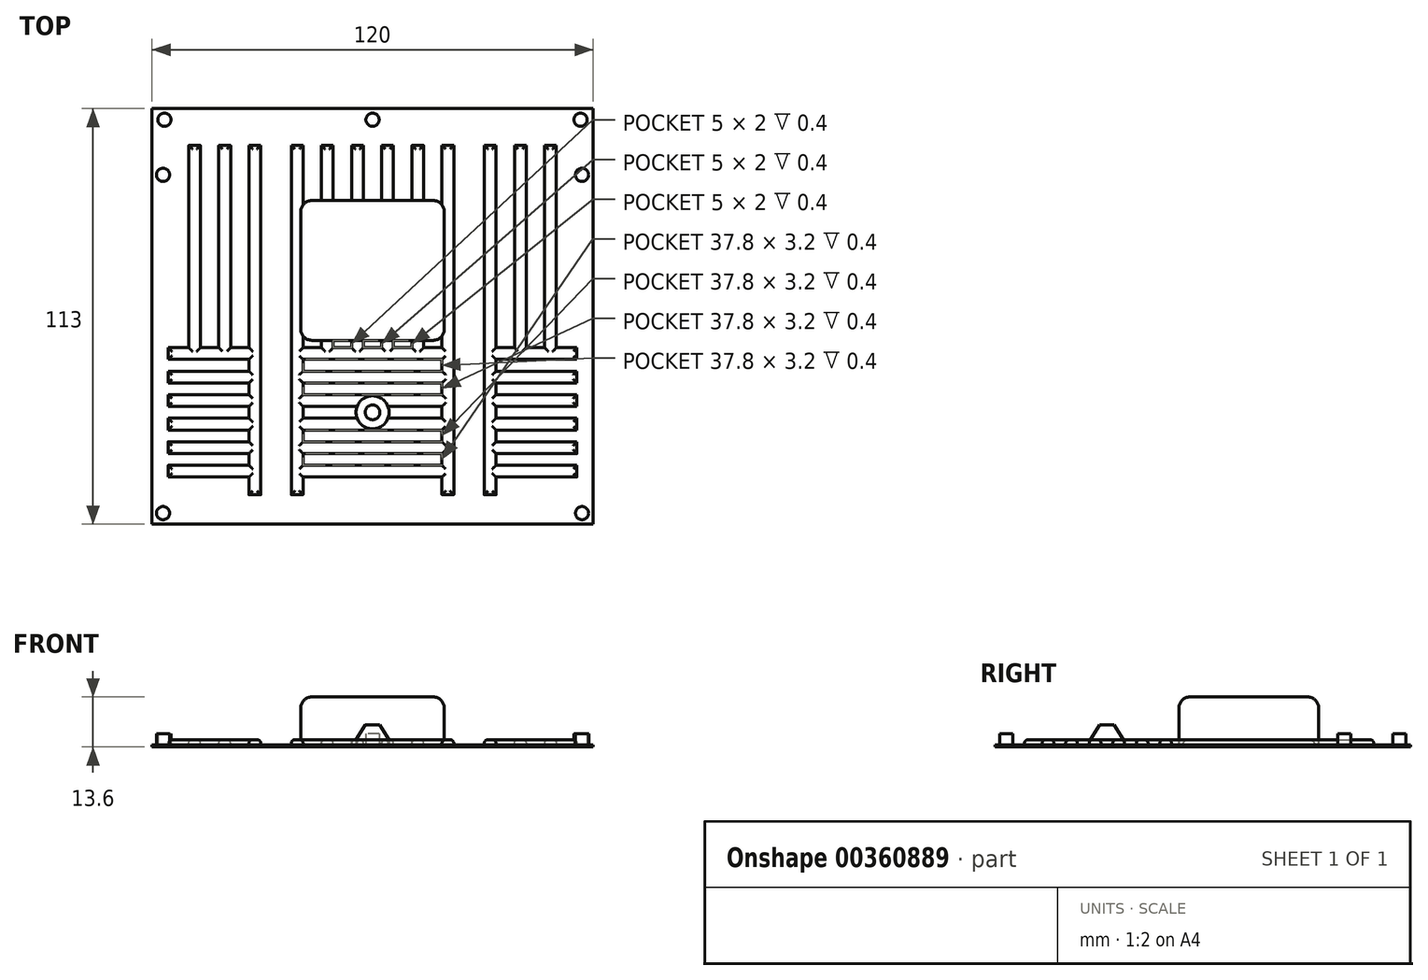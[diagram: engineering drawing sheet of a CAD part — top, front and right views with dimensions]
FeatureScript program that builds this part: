
annotation { "Feature Type Name" : "Feature", "Feature Type Description" : "" }
export const myFeature = defineFeature(function(context is Context, id is Id, definition is map)
    precondition{}
    {
        {
            var Q0;
            Q0=qCreatedBy(makeId("Top.planeOp"),FACE);
            var sketch = newSketch(context, id + "F0", { "sketchPlane" : qUnion([Q0])});
            skLineSegment(sketch, "E0.bottom", {"start": v(-60, 0) * mm, "end": v(60, 0) * mm});
            skLineSegment(sketch, "E0.top", {"start": v(-60, -113) * mm, "end": v(60, -113) * mm});
            skLineSegment(sketch, "E0.left", {"start": v(-60, 0) * mm, "end": v(-60, -113) * mm});
            skLineSegment(sketch, "E0.right", {"start": v(60, 0) * mm, "end": v(60, -113) * mm});
            skPoint(sketch, "E1", {"position": v(0, 0) * mm});
            skSolve(sketch);
        }
        {
            var Q0;
            Q0 = qSketchRegion(id + "F0", true);
            extrude(context, id + "F1", {"entities" : qUnion([Q0]), "depth" : 0.6 * mm});
        }
        {
            var Q0;
            Q0=qCreatedBy(makeId("Front.planeOp"),FACE);
            cPlane(context, id + "F2", {"entities" : qUnion([Q0]), "cplaneType" : CPlaneType.OFFSET, "offset" : 10 * mm, "width" : 150 * mm, "height" : 150 * mm});
        }
        {
            var Q0;
            {var subQ37=sQuery(id+"F0.wireOp",EDGE,"E0.bottom");var subQ42=sQuery(id+"F0.wireOp",EDGE,"E0.right");var subQ43=sQuery(id+"F0.wireOp",EDGE,"E0.top");var subQ45=sQuery(id+"F0.wireOp",EDGE,"E0.left");Q0=makeQuery(id+"F12.boolean.opBoolean","SPLIT",FACE,{"disambiguationData":[TD([makeQuery(id+"F1.opExtrude","SWEPT_FACE",FACE,{"disambiguationData":[OSD([subQ37])]})])],"derivedFrom":makeQuery(id+"F1.opExtrude","CAP_FACE",FACE,{"disambiguationData":[OSD([subQ37,subQ43,subQ45,subQ42])],"isStart":false})});}
            var sketch = newSketch(context, id + "F3", { "sketchPlane" : qUnion([Q0])});
            skLineSegment(sketch, "E2.bottom", {"start": v(-19.5, -25) * mm, "end": v(19.5, -25) * mm});
            skLineSegment(sketch, "E2.top", {"start": v(-19.5, -63) * mm, "end": v(19.5, -63) * mm});
            skLineSegment(sketch, "E2.left", {"start": v(-19.5, -25) * mm, "end": v(-19.5, -63) * mm});
            skLineSegment(sketch, "E2.right", {"start": v(19.5, -25) * mm, "end": v(19.5, -63) * mm});
            skSolve(sketch);
        }
        {
            var Q0;
            Q0=qCreatedBy(id+"F2.planeOp",FACE);
            var sketch = newSketch(context, id + "F4", { "sketchPlane" : qUnion([Q0])});
            skLineSegment(sketch, "E3.bottom", {"start": v(50, 0.6) * mm, "end": v(46.8, 0.6) * mm});
            skLineSegment(sketch, "E3.top", {"start": v(50, 2) * mm, "end": v(46.8, 2) * mm});
            skLineSegment(sketch, "E3.left", {"start": v(50, 0.6) * mm, "end": v(50, 2) * mm});
            skLineSegment(sketch, "E3.right", {"start": v(46.8, 0.6) * mm, "end": v(46.8, 2) * mm});
            skLineSegment(sketch, "E4.bottom", {"start": v(41.8, 2) * mm, "end": v(38.6, 2) * mm});
            skLineSegment(sketch, "E4.top", {"start": v(41.8, 0.6) * mm, "end": v(38.6, 0.6) * mm});
            skLineSegment(sketch, "E4.left", {"start": v(41.8, 2) * mm, "end": v(41.8, 0.6) * mm});
            skLineSegment(sketch, "E4.right", {"start": v(38.6, 2) * mm, "end": v(38.6, 0.6) * mm});
            skLineSegment(sketch, "E5.bottom", {"start": v(33.6, 2) * mm, "end": v(30.4, 2) * mm});
            skLineSegment(sketch, "E5.top", {"start": v(33.6, 0.6) * mm, "end": v(30.4, 0.6) * mm});
            skLineSegment(sketch, "E5.left", {"start": v(33.6, 2) * mm, "end": v(33.6, 0.6) * mm});
            skLineSegment(sketch, "E5.right", {"start": v(30.4, 2) * mm, "end": v(30.4, 0.6) * mm});
            skLineSegment(sketch, "E6.bottom", {"start": v(-46.8, 2) * mm, "end": v(-50, 2) * mm});
            skLineSegment(sketch, "E6.top", {"start": v(-46.8, 0.6) * mm, "end": v(-50, 0.6) * mm});
            skLineSegment(sketch, "E6.left", {"start": v(-46.8, 2) * mm, "end": v(-46.8, 0.6) * mm});
            skLineSegment(sketch, "E6.right", {"start": v(-50, 2) * mm, "end": v(-50, 0.6) * mm});
            skLineSegment(sketch, "E7.bottom", {"start": v(-38.6, 2) * mm, "end": v(-41.8, 2) * mm});
            skLineSegment(sketch, "E7.top", {"start": v(-38.6, 0.6) * mm, "end": v(-41.8, 0.6) * mm});
            skLineSegment(sketch, "E7.left", {"start": v(-38.6, 2) * mm, "end": v(-38.6, 0.6) * mm});
            skLineSegment(sketch, "E7.right", {"start": v(-41.8, 2) * mm, "end": v(-41.8, 0.6) * mm});
            skLineSegment(sketch, "E8.bottom", {"start": v(-30.4, 2) * mm, "end": v(-33.6, 2) * mm});
            skLineSegment(sketch, "E8.top", {"start": v(-30.4, 0.6) * mm, "end": v(-33.6, 0.6) * mm});
            skLineSegment(sketch, "E8.left", {"start": v(-30.4, 2) * mm, "end": v(-30.4, 0.6) * mm});
            skLineSegment(sketch, "E8.right", {"start": v(-33.6, 2) * mm, "end": v(-33.6, 0.6) * mm});
            skLineSegment(sketch, "E9.bottom", {"start": v(-2.5, 2) * mm, "end": v(-5.7, 2) * mm});
            skLineSegment(sketch, "E9.top", {"start": v(-2.5, 0.6) * mm, "end": v(-5.7, 0.6) * mm});
            skLineSegment(sketch, "E9.left", {"start": v(-2.5, 2) * mm, "end": v(-2.5, 0.6) * mm});
            skLineSegment(sketch, "E9.right", {"start": v(-5.7, 2) * mm, "end": v(-5.7, 0.6) * mm});
            skLineSegment(sketch, "E10.bottom", {"start": v(-10.7, 2) * mm, "end": v(-13.9, 2) * mm});
            skLineSegment(sketch, "E10.top", {"start": v(-10.7, 0.6) * mm, "end": v(-13.9, 0.6) * mm});
            skLineSegment(sketch, "E10.left", {"start": v(-10.7, 2) * mm, "end": v(-10.7, 0.6) * mm});
            skLineSegment(sketch, "E10.right", {"start": v(-13.9, 2) * mm, "end": v(-13.9, 0.6) * mm});
            skLineSegment(sketch, "E11.bottom", {"start": v(-18.9, 2) * mm, "end": v(-22.1, 2) * mm});
            skLineSegment(sketch, "E11.top", {"start": v(-18.9, 0.6) * mm, "end": v(-22.1, 0.6) * mm});
            skLineSegment(sketch, "E11.left", {"start": v(-18.9, 2) * mm, "end": v(-18.9, 0.6) * mm});
            skLineSegment(sketch, "E11.right", {"start": v(-22.1, 2) * mm, "end": v(-22.1, 0.6) * mm});
            skLineSegment(sketch, "E12.bottom", {"start": v(5.7, 2) * mm, "end": v(2.5, 2) * mm});
            skLineSegment(sketch, "E12.top", {"start": v(5.7, 0.6) * mm, "end": v(2.5, 0.6) * mm});
            skLineSegment(sketch, "E12.left", {"start": v(5.7, 2) * mm, "end": v(5.7, 0.6) * mm});
            skLineSegment(sketch, "E12.right", {"start": v(2.5, 2) * mm, "end": v(2.5, 0.6) * mm});
            skLineSegment(sketch, "E13.bottom", {"start": v(13.9, 2) * mm, "end": v(10.7, 2) * mm});
            skLineSegment(sketch, "E13.top", {"start": v(13.9, 0.6) * mm, "end": v(10.7, 0.6) * mm});
            skLineSegment(sketch, "E13.left", {"start": v(13.9, 2) * mm, "end": v(13.9, 0.6) * mm});
            skLineSegment(sketch, "E13.right", {"start": v(10.7, 2) * mm, "end": v(10.7, 0.6) * mm});
            skLineSegment(sketch, "E14.bottom", {"start": v(22.1, 2) * mm, "end": v(18.9, 2) * mm});
            skLineSegment(sketch, "E14.top", {"start": v(22.1, 0.6) * mm, "end": v(18.9, 0.6) * mm});
            skLineSegment(sketch, "E14.left", {"start": v(22.1, 2) * mm, "end": v(22.1, 0.6) * mm});
            skLineSegment(sketch, "E14.right", {"start": v(18.9, 2) * mm, "end": v(18.9, 0.6) * mm});
            skSolve(sketch);
        }
        {
            var Q0;
            Q0 = qSketchRegion(id + "F4", true);
            extrude(context, id + "F5", {"entities" : qUnion([Q0]), "operationType" : NewBodyOperationType.ADD, "depth" : 55 * mm});
        }
        {
            var Q0;
            Q0=makeQuery(id+"F5.opExtrude","CAP_FACE",FACE,{"disambiguationData":[OSD([sQuery(id+"F4.wireOp",EDGE,"E8.bottom"),sQuery(id+"F4.wireOp",EDGE,"E8.top"),sQuery(id+"F4.wireOp",EDGE,"E8.left"),sQuery(id+"F4.wireOp",EDGE,"E8.right")])],"isStart":true});
            var Q1;
            Q1=makeQuery(id+"F5.opExtrude","CAP_FACE",FACE,{"disambiguationData":[OSD([sQuery(id+"F4.wireOp",EDGE,"E11.bottom"),sQuery(id+"F4.wireOp",EDGE,"E11.top"),sQuery(id+"F4.wireOp",EDGE,"E11.left"),sQuery(id+"F4.wireOp",EDGE,"E11.right")])],"isStart":true});
            var Q2;
            Q2=makeQuery(id+"F5.opExtrude","CAP_FACE",FACE,{"disambiguationData":[OSD([sQuery(id+"F4.wireOp",EDGE,"E14.bottom"),sQuery(id+"F4.wireOp",EDGE,"E14.top"),sQuery(id+"F4.wireOp",EDGE,"E14.left"),sQuery(id+"F4.wireOp",EDGE,"E14.right")])],"isStart":true});
            var Q3;
            Q3=makeQuery(id+"F5.opExtrude","CAP_FACE",FACE,{"disambiguationData":[OSD([sQuery(id+"F4.wireOp",EDGE,"E5.bottom"),sQuery(id+"F4.wireOp",EDGE,"E5.top"),sQuery(id+"F4.wireOp",EDGE,"E5.left"),sQuery(id+"F4.wireOp",EDGE,"E5.right")])],"isStart":true});
            extrude(context, id + "F6", {"entities" : qUnion([Q0, Q1, Q2, Q3]), "operationType" : NewBodyOperationType.ADD, "oppositeDirection" : true, "depth" : 95 * mm});
        }
        {
            var Q0;
            {var subQ0=sQuery(id+"F4.wireOp",EDGE,"E8.right");Q0=makeQuery(id+"F6.boolean.opBoolean","MERGE",FACE,{"derivedFrom":[makeQuery(id+"F5.opExtrude","SWEPT_FACE",FACE,{"disambiguationData":[OSD([subQ0])]}),makeQuery(id+"F6.opExtrude","SWEPT_FACE",FACE,{"disambiguationData":[OSD([subQ0])]})]});}
            var sketch = newSketch(context, id + "F7", { "sketchPlane" : qUnion([Q0])});
            skLineSegment(sketch, "E15.bottom", {"start": v(65, 2) * mm, "end": v(68.2, 2) * mm});
            skLineSegment(sketch, "E15.top", {"start": v(65, 0.6) * mm, "end": v(68.2, 0.6) * mm});
            skLineSegment(sketch, "E15.left", {"start": v(65, 2) * mm, "end": v(65, 0.6) * mm});
            skLineSegment(sketch, "E15.right", {"start": v(68.2, 2) * mm, "end": v(68.2, 0.6) * mm});
            skLineSegment(sketch, "E16.bottom", {"start": v(71.4, 2) * mm, "end": v(74.6, 2) * mm});
            skLineSegment(sketch, "E16.top", {"start": v(71.4, 0.6) * mm, "end": v(74.6, 0.6) * mm});
            skLineSegment(sketch, "E16.left", {"start": v(71.4, 2) * mm, "end": v(71.4, 0.6) * mm});
            skLineSegment(sketch, "E16.right", {"start": v(74.6, 2) * mm, "end": v(74.6, 0.6) * mm});
            skLineSegment(sketch, "E17.bottom", {"start": v(77.8, 2) * mm, "end": v(81, 2) * mm});
            skLineSegment(sketch, "E17.top", {"start": v(77.8, 0.6) * mm, "end": v(81, 0.6) * mm});
            skLineSegment(sketch, "E17.left", {"start": v(77.8, 2) * mm, "end": v(77.8, 0.6) * mm});
            skLineSegment(sketch, "E17.right", {"start": v(81, 2) * mm, "end": v(81, 0.6) * mm});
            skLineSegment(sketch, "E18.bottom", {"start": v(84.2, 2) * mm, "end": v(87.4, 2) * mm});
            skLineSegment(sketch, "E18.top", {"start": v(84.2, 0.6) * mm, "end": v(87.4, 0.6) * mm});
            skLineSegment(sketch, "E18.left", {"start": v(84.2, 2) * mm, "end": v(84.2, 0.6) * mm});
            skLineSegment(sketch, "E18.right", {"start": v(87.4, 2) * mm, "end": v(87.4, 0.6) * mm});
            skLineSegment(sketch, "E19.bottom", {"start": v(90.6, 2) * mm, "end": v(93.8, 2) * mm});
            skLineSegment(sketch, "E19.top", {"start": v(90.6, 0.6) * mm, "end": v(93.8, 0.6) * mm});
            skLineSegment(sketch, "E19.left", {"start": v(90.6, 2) * mm, "end": v(90.6, 0.6) * mm});
            skLineSegment(sketch, "E19.right", {"start": v(93.8, 2) * mm, "end": v(93.8, 0.6) * mm});
            skLineSegment(sketch, "E20.bottom", {"start": v(97, 2) * mm, "end": v(100.2, 2) * mm});
            skLineSegment(sketch, "E20.top", {"start": v(97, 0.6) * mm, "end": v(100.2, 0.6) * mm});
            skLineSegment(sketch, "E20.left", {"start": v(97, 2) * mm, "end": v(97, 0.6) * mm});
            skLineSegment(sketch, "E20.right", {"start": v(100.2, 2) * mm, "end": v(100.2, 0.6) * mm});
            skSolve(sketch);
        }
        {
            var Q0;
            Q0 = qSketchRegion(id + "F7", true);
            extrude(context, id + "F8", {"entities" : qUnion([Q0]), "operationType" : NewBodyOperationType.ADD, "depth" : 22 * mm});
        }
        {
            var Q0;
            {var subQ0=sQuery(id+"F4.wireOp",EDGE,"E5.left");Q0=makeQuery(id+"F6.boolean.opBoolean","MERGE",FACE,{"derivedFrom":[makeQuery(id+"F5.opExtrude","SWEPT_FACE",FACE,{"disambiguationData":[OSD([subQ0])]}),makeQuery(id+"F6.opExtrude","SWEPT_FACE",FACE,{"disambiguationData":[OSD([subQ0])]})]});}
            var sketch = newSketch(context, id + "F9", { "sketchPlane" : qUnion([Q0])});
            skLineSegment(sketch, "E21.bottom", {"start": v(-65, 0.6) * mm, "end": v(-68.2, 0.6) * mm});
            skLineSegment(sketch, "E21.top", {"start": v(-65, 2) * mm, "end": v(-68.2, 2) * mm});
            skLineSegment(sketch, "E21.left", {"start": v(-65, 0.6) * mm, "end": v(-65, 2) * mm});
            skLineSegment(sketch, "E21.right", {"start": v(-68.2, 0.6) * mm, "end": v(-68.2, 2) * mm});
            skLineSegment(sketch, "E22.bottom", {"start": v(-71.4, 0.6) * mm, "end": v(-74.6, 0.6) * mm});
            skLineSegment(sketch, "E22.top", {"start": v(-71.4, 2) * mm, "end": v(-74.6, 2) * mm});
            skLineSegment(sketch, "E22.left", {"start": v(-71.4, 0.6) * mm, "end": v(-71.4, 2) * mm});
            skLineSegment(sketch, "E22.right", {"start": v(-74.6, 0.6) * mm, "end": v(-74.6, 2) * mm});
            skLineSegment(sketch, "E23.bottom", {"start": v(-77.8, 0.6) * mm, "end": v(-81, 0.6) * mm});
            skLineSegment(sketch, "E23.top", {"start": v(-77.8, 2) * mm, "end": v(-81, 2) * mm});
            skLineSegment(sketch, "E23.left", {"start": v(-77.8, 0.6) * mm, "end": v(-77.8, 2) * mm});
            skLineSegment(sketch, "E23.right", {"start": v(-81, 0.6) * mm, "end": v(-81, 2) * mm});
            skLineSegment(sketch, "E24.bottom", {"start": v(-84.2, 0.6) * mm, "end": v(-87.4, 0.6) * mm});
            skLineSegment(sketch, "E24.top", {"start": v(-84.2, 2) * mm, "end": v(-87.4, 2) * mm});
            skLineSegment(sketch, "E24.left", {"start": v(-84.2, 0.6) * mm, "end": v(-84.2, 2) * mm});
            skLineSegment(sketch, "E24.right", {"start": v(-87.4, 0.6) * mm, "end": v(-87.4, 2) * mm});
            skLineSegment(sketch, "E25.bottom", {"start": v(-90.6, 0.6) * mm, "end": v(-93.8, 0.6) * mm});
            skLineSegment(sketch, "E25.top", {"start": v(-90.6, 2) * mm, "end": v(-93.8, 2) * mm});
            skLineSegment(sketch, "E25.left", {"start": v(-90.6, 0.6) * mm, "end": v(-90.6, 2) * mm});
            skLineSegment(sketch, "E25.right", {"start": v(-93.8, 0.6) * mm, "end": v(-93.8, 2) * mm});
            skLineSegment(sketch, "E26.bottom", {"start": v(-97, 0.6) * mm, "end": v(-100.2, 0.6) * mm});
            skLineSegment(sketch, "E26.top", {"start": v(-97, 2) * mm, "end": v(-100.2, 2) * mm});
            skLineSegment(sketch, "E26.left", {"start": v(-97, 0.6) * mm, "end": v(-97, 2) * mm});
            skLineSegment(sketch, "E26.right", {"start": v(-100.2, 0.6) * mm, "end": v(-100.2, 2) * mm});
            skSolve(sketch);
        }
        {
            var Q0;
            Q0 = qSketchRegion(id + "F9", true);
            extrude(context, id + "F10", {"entities" : qUnion([Q0]), "operationType" : NewBodyOperationType.ADD, "depth" : 22 * mm});
        }
        {
            var Q0;
            {var subQ0=sQuery(id+"F4.wireOp",EDGE,"E11.left");Q0=makeQuery(id+"F6.boolean.opBoolean","MERGE",FACE,{"derivedFrom":[makeQuery(id+"F5.opExtrude","SWEPT_FACE",FACE,{"disambiguationData":[OSD([subQ0])]}),makeQuery(id+"F6.opExtrude","SWEPT_FACE",FACE,{"disambiguationData":[OSD([subQ0])]})]});}
            var sketch = newSketch(context, id + "F11", { "sketchPlane" : qUnion([Q0])});
            skLineSegment(sketch, "E27.bottom", {"start": v(-68.2, 2) * mm, "end": v(-65, 2) * mm});
            skLineSegment(sketch, "E27.top", {"start": v(-68.2, 0.6) * mm, "end": v(-65, 0.6) * mm});
            skLineSegment(sketch, "E27.left", {"start": v(-68.2, 2) * mm, "end": v(-68.2, 0.6) * mm});
            skLineSegment(sketch, "E27.right", {"start": v(-65, 2) * mm, "end": v(-65, 0.6) * mm});
            skLineSegment(sketch, "E28.bottom", {"start": v(-74.6, 2) * mm, "end": v(-71.4, 2) * mm});
            skLineSegment(sketch, "E28.top", {"start": v(-74.6, 0.6) * mm, "end": v(-71.4, 0.6) * mm});
            skLineSegment(sketch, "E28.left", {"start": v(-74.6, 2) * mm, "end": v(-74.6, 0.6) * mm});
            skLineSegment(sketch, "E28.right", {"start": v(-71.4, 2) * mm, "end": v(-71.4, 0.6) * mm});
            skLineSegment(sketch, "E29.bottom", {"start": v(-81, 2) * mm, "end": v(-77.8, 2) * mm});
            skLineSegment(sketch, "E29.top", {"start": v(-81, 0.6) * mm, "end": v(-77.8, 0.6) * mm});
            skLineSegment(sketch, "E29.left", {"start": v(-81, 2) * mm, "end": v(-81, 0.6) * mm});
            skLineSegment(sketch, "E29.right", {"start": v(-77.8, 2) * mm, "end": v(-77.8, 0.6) * mm});
            skLineSegment(sketch, "E30.bottom", {"start": v(-87.4, 2) * mm, "end": v(-84.2, 2) * mm});
            skLineSegment(sketch, "E30.top", {"start": v(-87.4, 0.6) * mm, "end": v(-84.2, 0.6) * mm});
            skLineSegment(sketch, "E30.left", {"start": v(-87.4, 2) * mm, "end": v(-87.4, 0.6) * mm});
            skLineSegment(sketch, "E30.right", {"start": v(-84.2, 2) * mm, "end": v(-84.2, 0.6) * mm});
            skLineSegment(sketch, "E31.bottom", {"start": v(-93.8, 2) * mm, "end": v(-90.6, 2) * mm});
            skLineSegment(sketch, "E31.top", {"start": v(-93.8, 0.6) * mm, "end": v(-90.6, 0.6) * mm});
            skLineSegment(sketch, "E31.left", {"start": v(-93.8, 2) * mm, "end": v(-93.8, 0.6) * mm});
            skLineSegment(sketch, "E31.right", {"start": v(-90.6, 2) * mm, "end": v(-90.6, 0.6) * mm});
            skLineSegment(sketch, "E32.bottom", {"start": v(-100.2, 2) * mm, "end": v(-97, 2) * mm});
            skLineSegment(sketch, "E32.top", {"start": v(-100.2, 0.6) * mm, "end": v(-97, 0.6) * mm});
            skLineSegment(sketch, "E32.left", {"start": v(-100.2, 2) * mm, "end": v(-100.2, 0.6) * mm});
            skLineSegment(sketch, "E32.right", {"start": v(-97, 2) * mm, "end": v(-97, 0.6) * mm});
            skSolve(sketch);
        }
        {
            var Q0;
            Q0 = qSketchRegion(id + "F11", true);
            extrude(context, id + "F12", {"entities" : qUnion([Q0]), "operationType" : NewBodyOperationType.ADD, "depth" : 38 * mm});
        }
        {
            var Q0;
            {var subQ0=sQuery(id+"F4.wireOp",EDGE,"E5.bottom");Q0=makeQuery(id+"F10.boolean.opBoolean","MERGE",FACE,{"derivedFrom":[makeQuery(id+"F5.opExtrude","SWEPT_FACE",FACE,{"disambiguationData":[OSD([sQuery(id+"F4.wireOp",EDGE,"E3.top")])]}),makeQuery(id+"F5.opExtrude","SWEPT_FACE",FACE,{"disambiguationData":[OSD([sQuery(id+"F4.wireOp",EDGE,"E4.bottom")])]}),makeQuery(id+"F6.boolean.opBoolean","MERGE",FACE,{"derivedFrom":[makeQuery(id+"F5.opExtrude","SWEPT_FACE",FACE,{"disambiguationData":[OSD([subQ0])]}),makeQuery(id+"F6.opExtrude","SWEPT_FACE",FACE,{"disambiguationData":[OSD([subQ0])]})]}),makeQuery(id+"F10.opExtrude","SWEPT_FACE",FACE,{"disambiguationData":[OSD([sQuery(id+"F9.wireOp",EDGE,"E21.top")])]}),makeQuery(id+"F10.opExtrude","SWEPT_FACE",FACE,{"disambiguationData":[OSD([sQuery(id+"F9.wireOp",EDGE,"E22.top")])]}),makeQuery(id+"F10.opExtrude","SWEPT_FACE",FACE,{"disambiguationData":[OSD([sQuery(id+"F9.wireOp",EDGE,"E23.top")])]}),makeQuery(id+"F10.opExtrude","SWEPT_FACE",FACE,{"disambiguationData":[OSD([sQuery(id+"F9.wireOp",EDGE,"E24.top")])]}),makeQuery(id+"F10.opExtrude","SWEPT_FACE",FACE,{"disambiguationData":[OSD([sQuery(id+"F9.wireOp",EDGE,"E25.top")])]}),makeQuery(id+"F10.opExtrude","SWEPT_FACE",FACE,{"disambiguationData":[OSD([sQuery(id+"F9.wireOp",EDGE,"E26.top")])]})]});}
            var Q1;
            {var subQ0=sQuery(id+"F4.wireOp",EDGE,"E8.bottom");Q1=makeQuery(id+"F8.boolean.opBoolean","MERGE",FACE,{"derivedFrom":[makeQuery(id+"F5.opExtrude","SWEPT_FACE",FACE,{"disambiguationData":[OSD([sQuery(id+"F4.wireOp",EDGE,"E6.bottom")])]}),makeQuery(id+"F5.opExtrude","SWEPT_FACE",FACE,{"disambiguationData":[OSD([sQuery(id+"F4.wireOp",EDGE,"E7.bottom")])]}),makeQuery(id+"F6.boolean.opBoolean","MERGE",FACE,{"derivedFrom":[makeQuery(id+"F5.opExtrude","SWEPT_FACE",FACE,{"disambiguationData":[OSD([subQ0])]}),makeQuery(id+"F6.opExtrude","SWEPT_FACE",FACE,{"disambiguationData":[OSD([subQ0])]})]}),makeQuery(id+"F8.opExtrude","SWEPT_FACE",FACE,{"disambiguationData":[OSD([sQuery(id+"F7.wireOp",EDGE,"E15.bottom")])]}),makeQuery(id+"F8.opExtrude","SWEPT_FACE",FACE,{"disambiguationData":[OSD([sQuery(id+"F7.wireOp",EDGE,"E16.bottom")])]}),makeQuery(id+"F8.opExtrude","SWEPT_FACE",FACE,{"disambiguationData":[OSD([sQuery(id+"F7.wireOp",EDGE,"E17.bottom")])]}),makeQuery(id+"F8.opExtrude","SWEPT_FACE",FACE,{"disambiguationData":[OSD([sQuery(id+"F7.wireOp",EDGE,"E18.bottom")])]}),makeQuery(id+"F8.opExtrude","SWEPT_FACE",FACE,{"disambiguationData":[OSD([sQuery(id+"F7.wireOp",EDGE,"E19.bottom")])]}),makeQuery(id+"F8.opExtrude","SWEPT_FACE",FACE,{"disambiguationData":[OSD([sQuery(id+"F7.wireOp",EDGE,"E20.bottom")])]})]});}
            fillet(context, id + "F13", {"entities" : qUnion([Q0, Q1]), "radius" : 1 * mm, "tangentPropagation" : true, "allowEdgeOverflow" : false});
        }
        {
            var Q0;
            {var subQ11=sQuery(id+"F4.wireOp",EDGE,"E14.bottom");var subQ12=sQuery(id+"F4.wireOp",EDGE,"E11.left");var subQ15=sQuery(id+"F4.wireOp",EDGE,"E11.bottom");Q0=makeQuery(id+"Fkwt5QVxKcjviMI_1.boolean.opBoolean","SPLIT",FACE,{"disambiguationData":[TD([makeQuery(id+"F5.opExtrude","SWEPT_FACE",FACE,{"disambiguationData":[OSD([subQ12])]})])],"derivedFrom":makeQuery(id+"F12.boolean.opBoolean","MERGE",FACE,{"derivedFrom":[makeQuery(id+"F5.opExtrude","SWEPT_FACE",FACE,{"disambiguationData":[OSD([sQuery(id+"F4.wireOp",EDGE,"E9.bottom")])]}),makeQuery(id+"F5.opExtrude","SWEPT_FACE",FACE,{"disambiguationData":[OSD([sQuery(id+"F4.wireOp",EDGE,"E10.bottom")])]}),makeQuery(id+"F5.opExtrude","SWEPT_FACE",FACE,{"disambiguationData":[OSD([sQuery(id+"F4.wireOp",EDGE,"E12.bottom")])]}),makeQuery(id+"F5.opExtrude","SWEPT_FACE",FACE,{"disambiguationData":[OSD([sQuery(id+"F4.wireOp",EDGE,"E13.bottom")])]}),makeQuery(id+"F6.boolean.opBoolean","MERGE",FACE,{"derivedFrom":[makeQuery(id+"F5.opExtrude","SWEPT_FACE",FACE,{"disambiguationData":[OSD([subQ15])]}),makeQuery(id+"F6.opExtrude","SWEPT_FACE",FACE,{"disambiguationData":[OSD([subQ15])]})]}),makeQuery(id+"F6.boolean.opBoolean","MERGE",FACE,{"derivedFrom":[makeQuery(id+"F5.opExtrude","SWEPT_FACE",FACE,{"disambiguationData":[OSD([subQ11])]}),makeQuery(id+"F6.opExtrude","SWEPT_FACE",FACE,{"disambiguationData":[OSD([subQ11])]})]}),makeQuery(id+"F12.opExtrude","SWEPT_FACE",FACE,{"disambiguationData":[OSD([sQuery(id+"F11.wireOp",EDGE,"E27.bottom")])]}),makeQuery(id+"F12.opExtrude","SWEPT_FACE",FACE,{"disambiguationData":[OSD([sQuery(id+"F11.wireOp",EDGE,"E28.bottom")])]}),makeQuery(id+"F12.opExtrude","SWEPT_FACE",FACE,{"disambiguationData":[OSD([sQuery(id+"F11.wireOp",EDGE,"E29.bottom")])]}),makeQuery(id+"F12.opExtrude","SWEPT_FACE",FACE,{"disambiguationData":[OSD([sQuery(id+"F11.wireOp",EDGE,"E30.bottom")])]}),makeQuery(id+"F12.opExtrude","SWEPT_FACE",FACE,{"disambiguationData":[OSD([sQuery(id+"F11.wireOp",EDGE,"E31.bottom")])]}),makeQuery(id+"F12.opExtrude","SWEPT_FACE",FACE,{"disambiguationData":[OSD([sQuery(id+"F11.wireOp",EDGE,"E32.bottom")])]})]})});}
            var Q1;
            {var subQ0=sQuery(id+"F4.wireOp",EDGE,"E10.right");var subQ1=sQuery(id+"F4.wireOp",EDGE,"E10.left");var subQ2=sQuery(id+"F4.wireOp",EDGE,"E10.bottom");var subQ3=sQuery(id+"F4.wireOp",EDGE,"E14.bottom");var subQ4=sQuery(id+"F4.wireOp",EDGE,"E11.bottom");Q1=makeQuery(id+"Fkwt5QVxKcjviMI_1.boolean.opBoolean","SPLIT",FACE,{"disambiguationData":[TD([makeQuery(id+"F5.opExtrude","CAP_FACE",FACE,{"disambiguationData":[OSD([subQ2,sQuery(id+"F4.wireOp",EDGE,"E10.top"),subQ1,subQ0])],"isStart":true})])],"derivedFrom":makeQuery(id+"F12.boolean.opBoolean","MERGE",FACE,{"derivedFrom":[makeQuery(id+"F5.opExtrude","SWEPT_FACE",FACE,{"disambiguationData":[OSD([sQuery(id+"F4.wireOp",EDGE,"E9.bottom")])]}),makeQuery(id+"F5.opExtrude","SWEPT_FACE",FACE,{"disambiguationData":[OSD([subQ2])]}),makeQuery(id+"F5.opExtrude","SWEPT_FACE",FACE,{"disambiguationData":[OSD([sQuery(id+"F4.wireOp",EDGE,"E12.bottom")])]}),makeQuery(id+"F5.opExtrude","SWEPT_FACE",FACE,{"disambiguationData":[OSD([sQuery(id+"F4.wireOp",EDGE,"E13.bottom")])]}),makeQuery(id+"F6.boolean.opBoolean","MERGE",FACE,{"derivedFrom":[makeQuery(id+"F5.opExtrude","SWEPT_FACE",FACE,{"disambiguationData":[OSD([subQ4])]}),makeQuery(id+"F6.opExtrude","SWEPT_FACE",FACE,{"disambiguationData":[OSD([subQ4])]})]}),makeQuery(id+"F6.boolean.opBoolean","MERGE",FACE,{"derivedFrom":[makeQuery(id+"F5.opExtrude","SWEPT_FACE",FACE,{"disambiguationData":[OSD([subQ3])]}),makeQuery(id+"F6.opExtrude","SWEPT_FACE",FACE,{"disambiguationData":[OSD([subQ3])]})]}),makeQuery(id+"F12.opExtrude","SWEPT_FACE",FACE,{"disambiguationData":[OSD([sQuery(id+"F11.wireOp",EDGE,"E27.bottom")])]}),makeQuery(id+"F12.opExtrude","SWEPT_FACE",FACE,{"disambiguationData":[OSD([sQuery(id+"F11.wireOp",EDGE,"E28.bottom")])]}),makeQuery(id+"F12.opExtrude","SWEPT_FACE",FACE,{"disambiguationData":[OSD([sQuery(id+"F11.wireOp",EDGE,"E29.bottom")])]}),makeQuery(id+"F12.opExtrude","SWEPT_FACE",FACE,{"disambiguationData":[OSD([sQuery(id+"F11.wireOp",EDGE,"E30.bottom")])]}),makeQuery(id+"F12.opExtrude","SWEPT_FACE",FACE,{"disambiguationData":[OSD([sQuery(id+"F11.wireOp",EDGE,"E31.bottom")])]}),makeQuery(id+"F12.opExtrude","SWEPT_FACE",FACE,{"disambiguationData":[OSD([sQuery(id+"F11.wireOp",EDGE,"E32.bottom")])]})]})});}
            var Q2;
            {var subQ0=sQuery(id+"F4.wireOp",EDGE,"E9.right");var subQ1=sQuery(id+"F4.wireOp",EDGE,"E9.left");var subQ2=sQuery(id+"F4.wireOp",EDGE,"E9.bottom");var subQ3=sQuery(id+"F4.wireOp",EDGE,"E14.bottom");var subQ4=sQuery(id+"F4.wireOp",EDGE,"E11.bottom");Q2=makeQuery(id+"Fkwt5QVxKcjviMI_1.boolean.opBoolean","SPLIT",FACE,{"disambiguationData":[TD([makeQuery(id+"F5.opExtrude","CAP_FACE",FACE,{"disambiguationData":[OSD([subQ2,sQuery(id+"F4.wireOp",EDGE,"E9.top"),subQ1,subQ0])],"isStart":true})])],"derivedFrom":makeQuery(id+"F12.boolean.opBoolean","MERGE",FACE,{"derivedFrom":[makeQuery(id+"F5.opExtrude","SWEPT_FACE",FACE,{"disambiguationData":[OSD([subQ2])]}),makeQuery(id+"F5.opExtrude","SWEPT_FACE",FACE,{"disambiguationData":[OSD([sQuery(id+"F4.wireOp",EDGE,"E10.bottom")])]}),makeQuery(id+"F5.opExtrude","SWEPT_FACE",FACE,{"disambiguationData":[OSD([sQuery(id+"F4.wireOp",EDGE,"E12.bottom")])]}),makeQuery(id+"F5.opExtrude","SWEPT_FACE",FACE,{"disambiguationData":[OSD([sQuery(id+"F4.wireOp",EDGE,"E13.bottom")])]}),makeQuery(id+"F6.boolean.opBoolean","MERGE",FACE,{"derivedFrom":[makeQuery(id+"F5.opExtrude","SWEPT_FACE",FACE,{"disambiguationData":[OSD([subQ4])]}),makeQuery(id+"F6.opExtrude","SWEPT_FACE",FACE,{"disambiguationData":[OSD([subQ4])]})]}),makeQuery(id+"F6.boolean.opBoolean","MERGE",FACE,{"derivedFrom":[makeQuery(id+"F5.opExtrude","SWEPT_FACE",FACE,{"disambiguationData":[OSD([subQ3])]}),makeQuery(id+"F6.opExtrude","SWEPT_FACE",FACE,{"disambiguationData":[OSD([subQ3])]})]}),makeQuery(id+"F12.opExtrude","SWEPT_FACE",FACE,{"disambiguationData":[OSD([sQuery(id+"F11.wireOp",EDGE,"E27.bottom")])]}),makeQuery(id+"F12.opExtrude","SWEPT_FACE",FACE,{"disambiguationData":[OSD([sQuery(id+"F11.wireOp",EDGE,"E28.bottom")])]}),makeQuery(id+"F12.opExtrude","SWEPT_FACE",FACE,{"disambiguationData":[OSD([sQuery(id+"F11.wireOp",EDGE,"E29.bottom")])]}),makeQuery(id+"F12.opExtrude","SWEPT_FACE",FACE,{"disambiguationData":[OSD([sQuery(id+"F11.wireOp",EDGE,"E30.bottom")])]}),makeQuery(id+"F12.opExtrude","SWEPT_FACE",FACE,{"disambiguationData":[OSD([sQuery(id+"F11.wireOp",EDGE,"E31.bottom")])]}),makeQuery(id+"F12.opExtrude","SWEPT_FACE",FACE,{"disambiguationData":[OSD([sQuery(id+"F11.wireOp",EDGE,"E32.bottom")])]})]})});}
            var Q3;
            {var subQ0=sQuery(id+"F4.wireOp",EDGE,"E12.right");var subQ1=sQuery(id+"F4.wireOp",EDGE,"E12.left");var subQ2=sQuery(id+"F4.wireOp",EDGE,"E12.bottom");var subQ3=sQuery(id+"F4.wireOp",EDGE,"E14.bottom");var subQ4=sQuery(id+"F4.wireOp",EDGE,"E11.bottom");Q3=makeQuery(id+"Fkwt5QVxKcjviMI_1.boolean.opBoolean","SPLIT",FACE,{"disambiguationData":[TD([makeQuery(id+"F5.opExtrude","CAP_FACE",FACE,{"disambiguationData":[OSD([subQ2,sQuery(id+"F4.wireOp",EDGE,"E12.top"),subQ1,subQ0])],"isStart":true})])],"derivedFrom":makeQuery(id+"F12.boolean.opBoolean","MERGE",FACE,{"derivedFrom":[makeQuery(id+"F5.opExtrude","SWEPT_FACE",FACE,{"disambiguationData":[OSD([sQuery(id+"F4.wireOp",EDGE,"E9.bottom")])]}),makeQuery(id+"F5.opExtrude","SWEPT_FACE",FACE,{"disambiguationData":[OSD([sQuery(id+"F4.wireOp",EDGE,"E10.bottom")])]}),makeQuery(id+"F5.opExtrude","SWEPT_FACE",FACE,{"disambiguationData":[OSD([subQ2])]}),makeQuery(id+"F5.opExtrude","SWEPT_FACE",FACE,{"disambiguationData":[OSD([sQuery(id+"F4.wireOp",EDGE,"E13.bottom")])]}),makeQuery(id+"F6.boolean.opBoolean","MERGE",FACE,{"derivedFrom":[makeQuery(id+"F5.opExtrude","SWEPT_FACE",FACE,{"disambiguationData":[OSD([subQ4])]}),makeQuery(id+"F6.opExtrude","SWEPT_FACE",FACE,{"disambiguationData":[OSD([subQ4])]})]}),makeQuery(id+"F6.boolean.opBoolean","MERGE",FACE,{"derivedFrom":[makeQuery(id+"F5.opExtrude","SWEPT_FACE",FACE,{"disambiguationData":[OSD([subQ3])]}),makeQuery(id+"F6.opExtrude","SWEPT_FACE",FACE,{"disambiguationData":[OSD([subQ3])]})]}),makeQuery(id+"F12.opExtrude","SWEPT_FACE",FACE,{"disambiguationData":[OSD([sQuery(id+"F11.wireOp",EDGE,"E27.bottom")])]}),makeQuery(id+"F12.opExtrude","SWEPT_FACE",FACE,{"disambiguationData":[OSD([sQuery(id+"F11.wireOp",EDGE,"E28.bottom")])]}),makeQuery(id+"F12.opExtrude","SWEPT_FACE",FACE,{"disambiguationData":[OSD([sQuery(id+"F11.wireOp",EDGE,"E29.bottom")])]}),makeQuery(id+"F12.opExtrude","SWEPT_FACE",FACE,{"disambiguationData":[OSD([sQuery(id+"F11.wireOp",EDGE,"E30.bottom")])]}),makeQuery(id+"F12.opExtrude","SWEPT_FACE",FACE,{"disambiguationData":[OSD([sQuery(id+"F11.wireOp",EDGE,"E31.bottom")])]}),makeQuery(id+"F12.opExtrude","SWEPT_FACE",FACE,{"disambiguationData":[OSD([sQuery(id+"F11.wireOp",EDGE,"E32.bottom")])]})]})});}
            var Q4;
            {var subQ0=sQuery(id+"F4.wireOp",EDGE,"E13.right");var subQ1=sQuery(id+"F4.wireOp",EDGE,"E13.left");var subQ2=sQuery(id+"F4.wireOp",EDGE,"E13.bottom");var subQ3=sQuery(id+"F4.wireOp",EDGE,"E14.bottom");var subQ4=sQuery(id+"F4.wireOp",EDGE,"E11.bottom");Q4=makeQuery(id+"Fkwt5QVxKcjviMI_1.boolean.opBoolean","SPLIT",FACE,{"disambiguationData":[TD([makeQuery(id+"F5.opExtrude","CAP_FACE",FACE,{"disambiguationData":[OSD([subQ2,sQuery(id+"F4.wireOp",EDGE,"E13.top"),subQ1,subQ0])],"isStart":true})])],"derivedFrom":makeQuery(id+"F12.boolean.opBoolean","MERGE",FACE,{"derivedFrom":[makeQuery(id+"F5.opExtrude","SWEPT_FACE",FACE,{"disambiguationData":[OSD([sQuery(id+"F4.wireOp",EDGE,"E9.bottom")])]}),makeQuery(id+"F5.opExtrude","SWEPT_FACE",FACE,{"disambiguationData":[OSD([sQuery(id+"F4.wireOp",EDGE,"E10.bottom")])]}),makeQuery(id+"F5.opExtrude","SWEPT_FACE",FACE,{"disambiguationData":[OSD([sQuery(id+"F4.wireOp",EDGE,"E12.bottom")])]}),makeQuery(id+"F5.opExtrude","SWEPT_FACE",FACE,{"disambiguationData":[OSD([subQ2])]}),makeQuery(id+"F6.boolean.opBoolean","MERGE",FACE,{"derivedFrom":[makeQuery(id+"F5.opExtrude","SWEPT_FACE",FACE,{"disambiguationData":[OSD([subQ4])]}),makeQuery(id+"F6.opExtrude","SWEPT_FACE",FACE,{"disambiguationData":[OSD([subQ4])]})]}),makeQuery(id+"F6.boolean.opBoolean","MERGE",FACE,{"derivedFrom":[makeQuery(id+"F5.opExtrude","SWEPT_FACE",FACE,{"disambiguationData":[OSD([subQ3])]}),makeQuery(id+"F6.opExtrude","SWEPT_FACE",FACE,{"disambiguationData":[OSD([subQ3])]})]}),makeQuery(id+"F12.opExtrude","SWEPT_FACE",FACE,{"disambiguationData":[OSD([sQuery(id+"F11.wireOp",EDGE,"E27.bottom")])]}),makeQuery(id+"F12.opExtrude","SWEPT_FACE",FACE,{"disambiguationData":[OSD([sQuery(id+"F11.wireOp",EDGE,"E28.bottom")])]}),makeQuery(id+"F12.opExtrude","SWEPT_FACE",FACE,{"disambiguationData":[OSD([sQuery(id+"F11.wireOp",EDGE,"E29.bottom")])]}),makeQuery(id+"F12.opExtrude","SWEPT_FACE",FACE,{"disambiguationData":[OSD([sQuery(id+"F11.wireOp",EDGE,"E30.bottom")])]}),makeQuery(id+"F12.opExtrude","SWEPT_FACE",FACE,{"disambiguationData":[OSD([sQuery(id+"F11.wireOp",EDGE,"E31.bottom")])]}),makeQuery(id+"F12.opExtrude","SWEPT_FACE",FACE,{"disambiguationData":[OSD([sQuery(id+"F11.wireOp",EDGE,"E32.bottom")])]})]})});}
            fillet(context, id + "F14", {"entities" : qUnion([Q0, Q1, Q2, Q3, Q4]), "radius" : 1 * mm, "tangentPropagation" : true, "allowEdgeOverflow" : false});
        }
        {
            var Q0;
            {var subQ0=sQuery(id+"F4.wireOp",EDGE,"E14.right");var subQ1=makeQuery(id+"F5.opExtrude","SWEPT_FACE",FACE,{"disambiguationData":[OSD([subQ0])]});var subQ2=sQuery(id+"F7.wireOp",EDGE,"E20.right");var subQ3=makeQuery(id+"F8.opExtrude","SWEPT_FACE",FACE,{"disambiguationData":[OSD([subQ2])]});var subQ4=sQuery(id+"F9.wireOp",EDGE,"E22.right");var subQ5=makeQuery(id+"F10.opExtrude","SWEPT_FACE",FACE,{"disambiguationData":[OSD([subQ4])]});var subQ6=sQuery(id+"F4.wireOp",EDGE,"E14.left");var subQ7=sQuery(id+"F4.wireOp",EDGE,"E14.top");var subQ8=sQuery(id+"F4.wireOp",EDGE,"E14.bottom");var subQ9=makeQuery(id+"F5.opExtrude","CAP_FACE",FACE,{"disambiguationData":[OSD([subQ8,subQ7,subQ6,subQ0])],"isStart":true});var subQ10=sQuery(id+"F4.wireOp",EDGE,"E13.right");var subQ11=makeQuery(id+"F5.opExtrude","SWEPT_FACE",FACE,{"disambiguationData":[OSD([subQ10])]});var subQ12=sQuery(id+"F7.wireOp",EDGE,"E19.right");var subQ13=makeQuery(id+"F8.opExtrude","SWEPT_FACE",FACE,{"disambiguationData":[OSD([subQ12])]});var subQ14=sQuery(id+"F9.wireOp",EDGE,"E21.right");var subQ15=makeQuery(id+"F10.opExtrude","SWEPT_FACE",FACE,{"disambiguationData":[OSD([subQ14])]});var subQ16=sQuery(id+"F4.wireOp",EDGE,"E12.right");var subQ17=makeQuery(id+"F5.opExtrude","SWEPT_FACE",FACE,{"disambiguationData":[OSD([subQ16])]});var subQ18=sQuery(id+"F7.wireOp",EDGE,"E18.right");var subQ19=makeQuery(id+"F8.opExtrude","SWEPT_FACE",FACE,{"disambiguationData":[OSD([subQ18])]});var subQ20=sQuery(id+"F4.wireOp",EDGE,"E8.right");var subQ21=makeQuery(id+"F6.opExtrude","SWEPT_FACE",FACE,{"disambiguationData":[OSD([subQ20])]});var subQ22=sQuery(id+"F4.wireOp",EDGE,"E5.right");var subQ23=makeQuery(id+"F5.opExtrude","SWEPT_FACE",FACE,{"disambiguationData":[OSD([subQ22])]});var subQ24=sQuery(id+"F4.wireOp",EDGE,"E12.left");var subQ25=makeQuery(id+"F5.opExtrude","CAP_FACE",FACE,{"disambiguationData":[OSD([sQuery(id+"F4.wireOp",EDGE,"E12.bottom"),sQuery(id+"F4.wireOp",EDGE,"E12.top"),subQ24,subQ16])],"isStart":true});var subQ26=sQuery(id+"F4.wireOp",EDGE,"E11.right");var subQ27=makeQuery(id+"F5.opExtrude","SWEPT_FACE",FACE,{"disambiguationData":[OSD([subQ26])]});var subQ28=sQuery(id+"F7.wireOp",EDGE,"E17.right");var subQ29=makeQuery(id+"F8.opExtrude","SWEPT_FACE",FACE,{"disambiguationData":[OSD([subQ28])]});var subQ30=sQuery(id+"F4.wireOp",EDGE,"E11.left");var subQ31=sQuery(id+"F4.wireOp",EDGE,"E11.top");var subQ32=sQuery(id+"F4.wireOp",EDGE,"E11.bottom");var subQ33=makeQuery(id+"F5.opExtrude","CAP_FACE",FACE,{"disambiguationData":[OSD([subQ32,subQ31,subQ30,subQ26])],"isStart":true});var subQ34=sQuery(id+"F4.wireOp",EDGE,"E10.right");var subQ35=makeQuery(id+"F5.opExtrude","SWEPT_FACE",FACE,{"disambiguationData":[OSD([subQ34])]});var subQ36=sQuery(id+"F0.wireOp",EDGE,"E0.left");var subQ37=makeQuery(id+"F1.opExtrude","SWEPT_FACE",FACE,{"disambiguationData":[OSD([subQ36])]});var subQ38=sQuery(id+"F7.wireOp",EDGE,"E16.right");var subQ39=makeQuery(id+"F8.opExtrude","SWEPT_FACE",FACE,{"disambiguationData":[OSD([subQ38])]});var subQ40=sQuery(id+"F4.wireOp",EDGE,"E10.left");var subQ41=makeQuery(id+"F5.opExtrude","SWEPT_FACE",FACE,{"disambiguationData":[OSD([subQ40])]});var subQ42=sQuery(id+"F0.wireOp",EDGE,"E0.top");var subQ43=makeQuery(id+"F1.opExtrude","SWEPT_FACE",FACE,{"disambiguationData":[OSD([subQ42])]});var subQ44=sQuery(id+"F7.wireOp",EDGE,"E16.left");var subQ45=makeQuery(id+"F8.opExtrude","SWEPT_FACE",FACE,{"disambiguationData":[OSD([subQ44])]});var subQ46=makeQuery(id+"F5.opExtrude","CAP_FACE",FACE,{"disambiguationData":[OSD([sQuery(id+"F4.wireOp",EDGE,"E10.bottom"),sQuery(id+"F4.wireOp",EDGE,"E10.top"),subQ40,subQ34])],"isStart":true});var subQ47=sQuery(id+"F0.wireOp",EDGE,"E0.bottom");var subQ48=makeQuery(id+"F1.opExtrude","SWEPT_FACE",FACE,{"disambiguationData":[OSD([subQ47])]});var subQ49=sQuery(id+"F4.wireOp",EDGE,"E9.right");var subQ50=makeQuery(id+"F5.opExtrude","SWEPT_FACE",FACE,{"disambiguationData":[OSD([subQ49])]});var subQ51=sQuery(id+"F7.wireOp",EDGE,"E15.right");var subQ52=makeQuery(id+"F8.opExtrude","SWEPT_FACE",FACE,{"disambiguationData":[OSD([subQ51])]});var subQ53=sQuery(id+"F4.wireOp",EDGE,"E9.left");var subQ54=makeQuery(id+"F5.opExtrude","SWEPT_FACE",FACE,{"disambiguationData":[OSD([subQ53])]});var subQ55=sQuery(id+"F7.wireOp",EDGE,"E15.left");var subQ56=makeQuery(id+"F8.opExtrude","SWEPT_FACE",FACE,{"disambiguationData":[OSD([subQ55])]});var subQ57=makeQuery(id+"F5.opExtrude","CAP_FACE",FACE,{"disambiguationData":[OSD([sQuery(id+"F4.wireOp",EDGE,"E9.bottom"),sQuery(id+"F4.wireOp",EDGE,"E9.top"),subQ53,subQ49])],"isStart":true});var subQ58=sQuery(id+"F4.wireOp",EDGE,"E8.left");var subQ59=makeQuery(id+"F6.opExtrude","SWEPT_FACE",FACE,{"disambiguationData":[OSD([subQ58])]});var subQ60=sQuery(id+"F4.wireOp",EDGE,"E5.left");var subQ61=makeQuery(id+"F5.opExtrude","SWEPT_FACE",FACE,{"disambiguationData":[OSD([subQ60])]});var subQ62=sQuery(id+"F4.wireOp",EDGE,"E4.right");var subQ63=sQuery(id+"F4.wireOp",EDGE,"E4.left");var subQ64=makeQuery(id+"F5.opExtrude","CAP_FACE",FACE,{"disambiguationData":[OSD([sQuery(id+"F4.wireOp",EDGE,"E4.bottom"),sQuery(id+"F4.wireOp",EDGE,"E4.top"),subQ63,subQ62])],"isStart":true});var subQ65=makeQuery(id+"F6.opExtrude","SWEPT_FACE",FACE,{"disambiguationData":[OSD([subQ22])]});var subQ66=makeQuery(id+"F5.opExtrude","SWEPT_FACE",FACE,{"disambiguationData":[OSD([subQ30])]});var subQ67=sQuery(id+"F7.wireOp",EDGE,"E17.left");var subQ68=makeQuery(id+"F8.opExtrude","SWEPT_FACE",FACE,{"disambiguationData":[OSD([subQ67])]});var subQ69=sQuery(id+"F4.wireOp",EDGE,"E3.right");var subQ70=makeQuery(id+"F5.opExtrude","SWEPT_FACE",FACE,{"disambiguationData":[OSD([subQ69])]});var subQ71=sQuery(id+"F4.wireOp",EDGE,"E7.left");var subQ72=makeQuery(id+"F5.opExtrude","SWEPT_FACE",FACE,{"disambiguationData":[OSD([subQ71])]});var subQ73=makeQuery(id+"F6.opExtrude","SWEPT_FACE",FACE,{"disambiguationData":[OSD([subQ60])]});var subQ74=sQuery(id+"F4.wireOp",EDGE,"E5.top");var subQ75=sQuery(id+"F4.wireOp",EDGE,"E5.bottom");var subQ76=makeQuery(id+"F5.opExtrude","CAP_FACE",FACE,{"disambiguationData":[OSD([subQ75,subQ74,subQ60,subQ22])],"isStart":true});var subQ77=sQuery(id+"F4.wireOp",EDGE,"E3.left");var subQ78=makeQuery(id+"F5.opExtrude","SWEPT_FACE",FACE,{"disambiguationData":[OSD([subQ77])]});var subQ79=makeQuery(id+"F6.opExtrude","SWEPT_FACE",FACE,{"disambiguationData":[OSD([subQ30])]});var subQ80=sQuery(id+"F4.wireOp",EDGE,"E6.right");var subQ81=sQuery(id+"F4.wireOp",EDGE,"E6.left");var subQ82=makeQuery(id+"F5.opExtrude","CAP_FACE",FACE,{"disambiguationData":[OSD([sQuery(id+"F4.wireOp",EDGE,"E6.bottom"),sQuery(id+"F4.wireOp",EDGE,"E6.top"),subQ81,subQ80])],"isStart":true});var subQ83=makeQuery(id+"F5.opExtrude","SWEPT_FACE",FACE,{"disambiguationData":[OSD([subQ63])]});var subQ84=makeQuery(id+"F6.opExtrude","SWEPT_FACE",FACE,{"disambiguationData":[OSD([subQ26])]});var subQ85=makeQuery(id+"F5.opExtrude","SWEPT_FACE",FACE,{"disambiguationData":[OSD([subQ24])]});var subQ86=sQuery(id+"F7.wireOp",EDGE,"E18.left");var subQ87=makeQuery(id+"F8.opExtrude","SWEPT_FACE",FACE,{"disambiguationData":[OSD([subQ86])]});var subQ88=makeQuery(id+"F5.opExtrude","SWEPT_FACE",FACE,{"disambiguationData":[OSD([subQ62])]});var subQ89=makeQuery(id+"F5.opExtrude","SWEPT_FACE",FACE,{"disambiguationData":[OSD([subQ58])]});var subQ90=sQuery(id+"F0.wireOp",EDGE,"E0.right");var subQ91=makeQuery(id+"F1.opExtrude","SWEPT_FACE",FACE,{"disambiguationData":[OSD([subQ90])]});var subQ92=makeQuery(id+"F5.opExtrude","CAP_FACE",FACE,{"disambiguationData":[OSD([sQuery(id+"F4.wireOp",EDGE,"E3.bottom"),sQuery(id+"F4.wireOp",EDGE,"E3.top"),subQ77,subQ69])],"isStart":true});var subQ93=sQuery(id+"F4.wireOp",EDGE,"E13.left");var subQ94=makeQuery(id+"F5.opExtrude","CAP_FACE",FACE,{"disambiguationData":[OSD([sQuery(id+"F4.wireOp",EDGE,"E13.bottom"),sQuery(id+"F4.wireOp",EDGE,"E13.top"),subQ93,subQ10])],"isStart":true});var subQ95=makeQuery(id+"F5.opExtrude","SWEPT_FACE",FACE,{"disambiguationData":[OSD([subQ93])]});var subQ96=sQuery(id+"F7.wireOp",EDGE,"E19.left");var subQ97=makeQuery(id+"F8.opExtrude","SWEPT_FACE",FACE,{"disambiguationData":[OSD([subQ96])]});var subQ98=sQuery(id+"F9.wireOp",EDGE,"E21.left");var subQ99=makeQuery(id+"F10.opExtrude","SWEPT_FACE",FACE,{"disambiguationData":[OSD([subQ98])]});var subQ100=makeQuery(id+"F5.opExtrude","SWEPT_FACE",FACE,{"disambiguationData":[OSD([subQ81])]});var subQ101=makeQuery(id+"F6.opExtrude","SWEPT_FACE",FACE,{"disambiguationData":[OSD([subQ6])]});var subQ102=makeQuery(id+"F5.opExtrude","SWEPT_FACE",FACE,{"disambiguationData":[OSD([subQ6])]});var subQ103=sQuery(id+"F7.wireOp",EDGE,"E20.left");var subQ104=makeQuery(id+"F8.opExtrude","SWEPT_FACE",FACE,{"disambiguationData":[OSD([subQ103])]});var subQ105=sQuery(id+"F9.wireOp",EDGE,"E22.left");var subQ106=makeQuery(id+"F10.opExtrude","SWEPT_FACE",FACE,{"disambiguationData":[OSD([subQ105])]});var subQ107=makeQuery(id+"F5.opExtrude","SWEPT_FACE",FACE,{"disambiguationData":[OSD([subQ80])]});var subQ108=makeQuery(id+"F6.opExtrude","SWEPT_FACE",FACE,{"disambiguationData":[OSD([subQ0])]});var subQ109=sQuery(id+"F4.wireOp",EDGE,"E7.right");var subQ110=makeQuery(id+"F5.opExtrude","CAP_FACE",FACE,{"disambiguationData":[OSD([sQuery(id+"F4.wireOp",EDGE,"E7.bottom"),sQuery(id+"F4.wireOp",EDGE,"E7.top"),subQ71,subQ109])],"isStart":true});var subQ111=makeQuery(id+"F6.opExtrude","CAP_FACE",FACE,{"disambiguationData":[OSD([subQ75,subQ74,subQ60,subQ22])],"isStart":false});var subQ112=makeQuery(id+"F5.opExtrude","SWEPT_FACE",FACE,{"disambiguationData":[OSD([subQ109])]});var subQ113=makeQuery(id+"F6.opExtrude","CAP_FACE",FACE,{"disambiguationData":[OSD([subQ32,subQ31,subQ30,subQ26])],"isStart":false});var subQ114=sQuery(id+"F4.wireOp",EDGE,"E8.top");var subQ115=sQuery(id+"F4.wireOp",EDGE,"E8.bottom");var subQ116=makeQuery(id+"F5.opExtrude","CAP_FACE",FACE,{"disambiguationData":[OSD([subQ115,subQ114,subQ58,subQ20])],"isStart":true});var subQ117=makeQuery(id+"F6.opExtrude","CAP_FACE",FACE,{"disambiguationData":[OSD([subQ8,subQ7,subQ6,subQ0])],"isStart":false});var subQ118=makeQuery(id+"F5.opExtrude","SWEPT_FACE",FACE,{"disambiguationData":[OSD([subQ20])]});var subQ119=makeQuery(id+"F6.opExtrude","CAP_FACE",FACE,{"disambiguationData":[OSD([subQ115,subQ114,subQ58,subQ20])],"isStart":false});var subQ120=makeQuery(id+"F8.opExtrude","CAP_FACE",FACE,{"disambiguationData":[OSD([sQuery(id+"F7.wireOp",EDGE,"E15.bottom"),sQuery(id+"F7.wireOp",EDGE,"E15.top"),subQ55,subQ51])],"isStart":false});var subQ121=makeQuery(id+"F8.opExtrude","CAP_FACE",FACE,{"disambiguationData":[OSD([sQuery(id+"F7.wireOp",EDGE,"E16.bottom"),sQuery(id+"F7.wireOp",EDGE,"E16.top"),subQ44,subQ38])],"isStart":false});var subQ122=makeQuery(id+"F8.opExtrude","CAP_FACE",FACE,{"disambiguationData":[OSD([sQuery(id+"F7.wireOp",EDGE,"E17.bottom"),sQuery(id+"F7.wireOp",EDGE,"E17.top"),subQ67,subQ28])],"isStart":false});var subQ123=makeQuery(id+"F8.opExtrude","CAP_FACE",FACE,{"disambiguationData":[OSD([sQuery(id+"F7.wireOp",EDGE,"E18.bottom"),sQuery(id+"F7.wireOp",EDGE,"E18.top"),subQ86,subQ18])],"isStart":false});var subQ124=makeQuery(id+"F8.opExtrude","CAP_FACE",FACE,{"disambiguationData":[OSD([sQuery(id+"F7.wireOp",EDGE,"E19.bottom"),sQuery(id+"F7.wireOp",EDGE,"E19.top"),subQ96,subQ12])],"isStart":false});var subQ125=makeQuery(id+"F10.opExtrude","CAP_FACE",FACE,{"disambiguationData":[OSD([sQuery(id+"F9.wireOp",EDGE,"E21.bottom"),sQuery(id+"F9.wireOp",EDGE,"E21.top"),subQ98,subQ14])],"isStart":false});var subQ126=makeQuery(id+"F8.opExtrude","CAP_FACE",FACE,{"disambiguationData":[OSD([sQuery(id+"F7.wireOp",EDGE,"E20.bottom"),sQuery(id+"F7.wireOp",EDGE,"E20.top"),subQ103,subQ2])],"isStart":false});var subQ127=makeQuery(id+"F10.opExtrude","CAP_FACE",FACE,{"disambiguationData":[OSD([sQuery(id+"F9.wireOp",EDGE,"E22.bottom"),sQuery(id+"F9.wireOp",EDGE,"E22.top"),subQ105,subQ4])],"isStart":false});var subQ128=sQuery(id+"F9.wireOp",EDGE,"E23.right");var subQ129=sQuery(id+"F9.wireOp",EDGE,"E23.left");var subQ130=makeQuery(id+"F10.opExtrude","CAP_FACE",FACE,{"disambiguationData":[OSD([sQuery(id+"F9.wireOp",EDGE,"E23.bottom"),sQuery(id+"F9.wireOp",EDGE,"E23.top"),subQ129,subQ128])],"isStart":false});var subQ131=makeQuery(id+"F10.opExtrude","SWEPT_FACE",FACE,{"disambiguationData":[OSD([subQ129])]});var subQ132=makeQuery(id+"F10.opExtrude","SWEPT_FACE",FACE,{"disambiguationData":[OSD([subQ128])]});var subQ133=sQuery(id+"F9.wireOp",EDGE,"E24.right");var subQ134=sQuery(id+"F9.wireOp",EDGE,"E24.left");var subQ135=makeQuery(id+"F10.opExtrude","CAP_FACE",FACE,{"disambiguationData":[OSD([sQuery(id+"F9.wireOp",EDGE,"E24.bottom"),sQuery(id+"F9.wireOp",EDGE,"E24.top"),subQ134,subQ133])],"isStart":false});var subQ136=makeQuery(id+"F10.opExtrude","SWEPT_FACE",FACE,{"disambiguationData":[OSD([subQ134])]});var subQ137=makeQuery(id+"F10.opExtrude","SWEPT_FACE",FACE,{"disambiguationData":[OSD([subQ133])]});var subQ138=sQuery(id+"F9.wireOp",EDGE,"E25.right");var subQ139=sQuery(id+"F9.wireOp",EDGE,"E25.left");var subQ140=makeQuery(id+"F10.opExtrude","CAP_FACE",FACE,{"disambiguationData":[OSD([sQuery(id+"F9.wireOp",EDGE,"E25.bottom"),sQuery(id+"F9.wireOp",EDGE,"E25.top"),subQ139,subQ138])],"isStart":false});var subQ141=makeQuery(id+"F10.opExtrude","SWEPT_FACE",FACE,{"disambiguationData":[OSD([subQ139])]});var subQ142=makeQuery(id+"F10.opExtrude","SWEPT_FACE",FACE,{"disambiguationData":[OSD([subQ138])]});var subQ143=sQuery(id+"F9.wireOp",EDGE,"E26.right");var subQ144=sQuery(id+"F9.wireOp",EDGE,"E26.left");var subQ145=makeQuery(id+"F10.opExtrude","CAP_FACE",FACE,{"disambiguationData":[OSD([sQuery(id+"F9.wireOp",EDGE,"E26.bottom"),sQuery(id+"F9.wireOp",EDGE,"E26.top"),subQ144,subQ143])],"isStart":false});var subQ146=makeQuery(id+"F10.opExtrude","SWEPT_FACE",FACE,{"disambiguationData":[OSD([subQ144])]});var subQ147=makeQuery(id+"F10.opExtrude","SWEPT_FACE",FACE,{"disambiguationData":[OSD([subQ143])]});var subQ148=makeQuery(id+"F12.opExtrude","SWEPT_FACE",FACE,{"disambiguationData":[OSD([sQuery(id+"F11.wireOp",EDGE,"E32.left")])]});Q0=makeQuery(id+"Fkwt5QVxKcjviMI_1.boolean.opBoolean","SPLIT",FACE,{"disambiguationData":[TD([subQ48,subQ43,subQ37,subQ91,subQ92,subQ78,subQ70,subQ64,subQ83,subQ88,subQ76,subQ61,subQ23,subQ82,subQ100,subQ107,subQ110,subQ72,subQ112,subQ116,subQ89,subQ118,subQ57,subQ54,subQ50,subQ46,subQ41,subQ35,subQ33,subQ66,subQ27,subQ25,subQ85,subQ17,subQ94,subQ95,subQ11,subQ9,subQ102,subQ1,subQ73,subQ65,subQ59,subQ21,subQ79,subQ84,subQ101,subQ108,subQ111,subQ119,subQ113,subQ117,subQ120,subQ56,subQ52,subQ121,subQ45,subQ39,subQ122,subQ68,subQ29,subQ123,subQ87,subQ19,subQ124,subQ97,subQ13,subQ126,subQ104,subQ3,subQ125,subQ99,subQ15,subQ127,subQ106,subQ5,subQ130,subQ131,subQ132,subQ135,subQ136,subQ137,subQ140,subQ141,subQ142,subQ145,subQ146,subQ147,subQ148,makeQuery(id+"Fkwt5QVxKcjviMI_1.opLoft","SWEPT_FACE",FACE,{"disambiguationData":[OSD([sQuery(id+"F3.wireOp",EDGE,"E2.bottom"),sQuery(id+"F3.wireOp",EDGE,"E2.left"),sQuery(id+"F3.wireOp",EDGE,"E2.right"),sQuery(id+"FE5xeYKwAuwMR8U_1.wireOp",EDGE,"wRlAwEkL-zv5v-XHx1-PrvH-ztm02dXU6yU6.bottom"),sQuery(id+"FE5xeYKwAuwMR8U_1.wireOp",EDGE,"wRlAwEkL-zv5v-XHx1-PrvH-ztm02dXU6yU6.left"),sQuery(id+"FE5xeYKwAuwMR8U_1.wireOp",EDGE,"wRlAwEkL-zv5v-XHx1-PrvH-ztm02dXU6yU6.right")])]})])],"derivedFrom":makeQuery(id+"F12.boolean.opBoolean","SPLIT",FACE,{"disambiguationData":[TD([subQ48])],"derivedFrom":makeQuery(id+"F1.opExtrude","CAP_FACE",FACE,{"disambiguationData":[OSD([subQ47,subQ42,subQ36,subQ90])],"isStart":false})})});}
            var sketch = newSketch(context, id + "F15", { "sketchPlane" : qUnion([Q0])});
            skCircle(sketch, "E33", {"center": v(0, -82.6) * mm, "radius": 4.5 * mm});
            skSolve(sketch);
        }
        {
            var Q0;
            Q0 = qSketchRegion(id + "F15", true);
            extrude(context, id + "F16", {"entities" : qUnion([Q0]), "operationType" : NewBodyOperationType.ADD, "depth" : 1.4 * mm});
        }
        {
            var Q0;
            {var subQ11=sQuery(id+"F4.wireOp",EDGE,"E14.bottom");var subQ12=sQuery(id+"F4.wireOp",EDGE,"E11.left");var subQ15=sQuery(id+"F4.wireOp",EDGE,"E11.bottom");Q0=makeQuery(id+"F16.boolean.opBoolean","MERGE",FACE,{"derivedFrom":[makeQuery(id+"F14.opFillet","SPLIT",FACE,{"disambiguationData":[OD(2.0)],"derivedFrom":makeQuery(id+"Fkwt5QVxKcjviMI_1.boolean.opBoolean","SPLIT",FACE,{"disambiguationData":[TD([makeQuery(id+"F5.opExtrude","SWEPT_FACE",FACE,{"disambiguationData":[OSD([subQ12])]})])],"derivedFrom":makeQuery(id+"F12.boolean.opBoolean","MERGE",FACE,{"derivedFrom":[makeQuery(id+"F5.opExtrude","SWEPT_FACE",FACE,{"disambiguationData":[OSD([sQuery(id+"F4.wireOp",EDGE,"E9.bottom")])]}),makeQuery(id+"F5.opExtrude","SWEPT_FACE",FACE,{"disambiguationData":[OSD([sQuery(id+"F4.wireOp",EDGE,"E10.bottom")])]}),makeQuery(id+"F5.opExtrude","SWEPT_FACE",FACE,{"disambiguationData":[OSD([sQuery(id+"F4.wireOp",EDGE,"E12.bottom")])]}),makeQuery(id+"F5.opExtrude","SWEPT_FACE",FACE,{"disambiguationData":[OSD([sQuery(id+"F4.wireOp",EDGE,"E13.bottom")])]}),makeQuery(id+"F6.boolean.opBoolean","MERGE",FACE,{"derivedFrom":[makeQuery(id+"F5.opExtrude","SWEPT_FACE",FACE,{"disambiguationData":[OSD([subQ15])]}),makeQuery(id+"F6.opExtrude","SWEPT_FACE",FACE,{"disambiguationData":[OSD([subQ15])]})]}),makeQuery(id+"F6.boolean.opBoolean","MERGE",FACE,{"derivedFrom":[makeQuery(id+"F5.opExtrude","SWEPT_FACE",FACE,{"disambiguationData":[OSD([subQ11])]}),makeQuery(id+"F6.opExtrude","SWEPT_FACE",FACE,{"disambiguationData":[OSD([subQ11])]})]}),makeQuery(id+"F12.opExtrude","SWEPT_FACE",FACE,{"disambiguationData":[OSD([sQuery(id+"F11.wireOp",EDGE,"E27.bottom")])]}),makeQuery(id+"F12.opExtrude","SWEPT_FACE",FACE,{"disambiguationData":[OSD([sQuery(id+"F11.wireOp",EDGE,"E28.bottom")])]}),makeQuery(id+"F12.opExtrude","SWEPT_FACE",FACE,{"disambiguationData":[OSD([sQuery(id+"F11.wireOp",EDGE,"E29.bottom")])]}),makeQuery(id+"F12.opExtrude","SWEPT_FACE",FACE,{"disambiguationData":[OSD([sQuery(id+"F11.wireOp",EDGE,"E30.bottom")])]}),makeQuery(id+"F12.opExtrude","SWEPT_FACE",FACE,{"disambiguationData":[OSD([sQuery(id+"F11.wireOp",EDGE,"E31.bottom")])]}),makeQuery(id+"F12.opExtrude","SWEPT_FACE",FACE,{"disambiguationData":[OSD([sQuery(id+"F11.wireOp",EDGE,"E32.bottom")])]})]})})}),makeQuery(id+"F16.opExtrude","CAP_FACE",FACE,{"disambiguationData":[OSD([sQuery(id+"F15.wireOp",EDGE,"E33")])],"isStart":false})]});}
            cPlane(context, id + "F17", {"entities" : qUnion([Q0]), "cplaneType" : CPlaneType.OFFSET, "offset" : 4 * mm, "width" : 150 * mm, "height" : 150 * mm});
        }
        {
            var Q0;
            Q0=qCreatedBy(id+"F17.planeOp",FACE);
            var sketch = newSketch(context, id + "F18", { "sketchPlane" : qUnion([Q0])});
            skCircle(sketch, "E34", {"center": v(0, -82.6) * mm, "radius": 2 * mm});
            skSolve(sketch);
        }
        {
            var Q0;
            {var subQ11=sQuery(id+"F4.wireOp",EDGE,"E14.bottom");var subQ12=sQuery(id+"F4.wireOp",EDGE,"E11.left");var subQ15=sQuery(id+"F4.wireOp",EDGE,"E11.bottom");Q0=makeQuery(id+"F16.boolean.opBoolean","MERGE",FACE,{"derivedFrom":[makeQuery(id+"F14.opFillet","SPLIT",FACE,{"disambiguationData":[OD(2.0)],"derivedFrom":makeQuery(id+"Fkwt5QVxKcjviMI_1.boolean.opBoolean","SPLIT",FACE,{"disambiguationData":[TD([makeQuery(id+"F5.opExtrude","SWEPT_FACE",FACE,{"disambiguationData":[OSD([subQ12])]})])],"derivedFrom":makeQuery(id+"F12.boolean.opBoolean","MERGE",FACE,{"derivedFrom":[makeQuery(id+"F5.opExtrude","SWEPT_FACE",FACE,{"disambiguationData":[OSD([sQuery(id+"F4.wireOp",EDGE,"E9.bottom")])]}),makeQuery(id+"F5.opExtrude","SWEPT_FACE",FACE,{"disambiguationData":[OSD([sQuery(id+"F4.wireOp",EDGE,"E10.bottom")])]}),makeQuery(id+"F5.opExtrude","SWEPT_FACE",FACE,{"disambiguationData":[OSD([sQuery(id+"F4.wireOp",EDGE,"E12.bottom")])]}),makeQuery(id+"F5.opExtrude","SWEPT_FACE",FACE,{"disambiguationData":[OSD([sQuery(id+"F4.wireOp",EDGE,"E13.bottom")])]}),makeQuery(id+"F6.boolean.opBoolean","MERGE",FACE,{"derivedFrom":[makeQuery(id+"F5.opExtrude","SWEPT_FACE",FACE,{"disambiguationData":[OSD([subQ15])]}),makeQuery(id+"F6.opExtrude","SWEPT_FACE",FACE,{"disambiguationData":[OSD([subQ15])]})]}),makeQuery(id+"F6.boolean.opBoolean","MERGE",FACE,{"derivedFrom":[makeQuery(id+"F5.opExtrude","SWEPT_FACE",FACE,{"disambiguationData":[OSD([subQ11])]}),makeQuery(id+"F6.opExtrude","SWEPT_FACE",FACE,{"disambiguationData":[OSD([subQ11])]})]}),makeQuery(id+"F12.opExtrude","SWEPT_FACE",FACE,{"disambiguationData":[OSD([sQuery(id+"F11.wireOp",EDGE,"E27.bottom")])]}),makeQuery(id+"F12.opExtrude","SWEPT_FACE",FACE,{"disambiguationData":[OSD([sQuery(id+"F11.wireOp",EDGE,"E28.bottom")])]}),makeQuery(id+"F12.opExtrude","SWEPT_FACE",FACE,{"disambiguationData":[OSD([sQuery(id+"F11.wireOp",EDGE,"E29.bottom")])]}),makeQuery(id+"F12.opExtrude","SWEPT_FACE",FACE,{"disambiguationData":[OSD([sQuery(id+"F11.wireOp",EDGE,"E30.bottom")])]}),makeQuery(id+"F12.opExtrude","SWEPT_FACE",FACE,{"disambiguationData":[OSD([sQuery(id+"F11.wireOp",EDGE,"E31.bottom")])]}),makeQuery(id+"F12.opExtrude","SWEPT_FACE",FACE,{"disambiguationData":[OSD([sQuery(id+"F11.wireOp",EDGE,"E32.bottom")])]})]})})}),makeQuery(id+"F16.opExtrude","CAP_FACE",FACE,{"disambiguationData":[OSD([sQuery(id+"F15.wireOp",EDGE,"E33")])],"isStart":false})]});}
            var sketch = newSketch(context, id + "F19", { "sketchPlane" : qUnion([Q0])});
            skCircle(sketch, "E35", {"center": v(0, -82.6) * mm, "radius": 4.5 * mm});
            skSolve(sketch);
        }
        {
            var Q1;
            {var subQ0=sQuery(id+"F19.wireOp",EDGE,"E35");var subQ1=makeQuery(id+"F12.opExtrude","SWEPT_FACE",FACE,{"disambiguationData":[OSD([sQuery(id+"F11.wireOp",EDGE,"E32.bottom")])]});var subQ2=sQuery(id+"F11.wireOp",EDGE,"E29.bottom");var subQ3=makeQuery(id+"F12.opExtrude","SWEPT_FACE",FACE,{"disambiguationData":[OSD([subQ2])]});var subQ4=sQuery(id+"F11.wireOp",EDGE,"E28.bottom");var subQ5=makeQuery(id+"F12.opExtrude","SWEPT_FACE",FACE,{"disambiguationData":[OSD([subQ4])]});var subQ6=makeQuery(id+"F12.opExtrude","SWEPT_FACE",FACE,{"disambiguationData":[OSD([sQuery(id+"F11.wireOp",EDGE,"E27.bottom")])]});var subQ7=sQuery(id+"F4.wireOp",EDGE,"E14.bottom");var subQ8=makeQuery(id+"F6.opExtrude","SWEPT_FACE",FACE,{"disambiguationData":[OSD([subQ7])]});var subQ9=sQuery(id+"F4.wireOp",EDGE,"E11.left");var subQ11=sQuery(id+"F4.wireOp",EDGE,"E11.bottom");var subQ12=makeQuery(id+"F5.opExtrude","SWEPT_FACE",FACE,{"disambiguationData":[OSD([subQ11])]});var subQ13=makeQuery(id+"F6.opExtrude","SWEPT_FACE",FACE,{"disambiguationData":[OSD([subQ11])]});var subQ15=makeQuery(id+"F12.opExtrude","SWEPT_FACE",FACE,{"disambiguationData":[OSD([sQuery(id+"F11.wireOp",EDGE,"E30.bottom")])]});var subQ18=makeQuery(id+"F5.opExtrude","SWEPT_FACE",FACE,{"disambiguationData":[OSD([subQ7])]});var subQ21=makeQuery(id+"F12.opExtrude","SWEPT_FACE",FACE,{"disambiguationData":[OSD([sQuery(id+"F11.wireOp",EDGE,"E31.bottom")])]});var subQ28=makeQuery(id+"F12.boolean.opBoolean","MERGE",FACE,{"derivedFrom":[makeQuery(id+"F6.boolean.opBoolean","MERGE",FACE,{"derivedFrom":[subQ12,subQ13]}),makeQuery(id+"F6.boolean.opBoolean","MERGE",FACE,{"derivedFrom":[subQ18,subQ8]}),subQ6,subQ5,subQ3,subQ15,subQ21,subQ1]});var subQ34=makeQuery(id+"F12.opExtrude","SWEPT_FACE",FACE,{"disambiguationData":[OSD([sQuery(id+"F11.wireOp",EDGE,"E27.left")])]});var subQ35=sQuery(id+"F11.wireOp",EDGE,"E28.right");var subQ38=makeQuery(id+"F14.opFillet","BLEND_EDGE",EDGE,{"blendedFrom":[makeQuery(id+"F12.opExtrude","SWEPT_EDGE",EDGE,{"disambiguationData":[OSD([subQ11,subQ9,subQ4,subQ35])]}),subQ28],"blendedInto":[subQ28]});var subQ40=sQuery(id+"F4.wireOp",EDGE,"E14.right");var subQ43=makeQuery(id+"F6.boolean.opBoolean","MERGE",EDGE,{"derivedFrom":[makeQuery(id+"F5.opExtrude","SWEPT_EDGE",EDGE,{"disambiguationData":[OSD([subQ7,subQ40])]}),makeQuery(id+"F6.opExtrude","SWEPT_EDGE",EDGE,{"disambiguationData":[OSD([subQ7,subQ40])]})]});var subQ44=makeQuery(id+"F19.imprint","INTERSECT",VERTEX,{"derivedFrom":[makeQuery(id+"F16.boolean.opBoolean","SPLIT",EDGE,{"disambiguationData":[TD([makeQuery(id+"F14.opFillet","BLEND_FACE",FACE,{"disambiguationData":[OSD([subQ7,subQ40]),TDD([makeQuery(id+"F12.boolean.opBoolean","SPLIT",EDGE,{"disambiguationData":[TD([subQ34])],"derivedFrom":subQ43})])]})])],"derivedFrom":subQ38}),subQ0]});Q1=makeQuery(id+"F19.imprint","IMPRINT",FACE,{"disambiguationData":[TD([[makeQuery(id+"F19.imprint","IMPRINT",EDGE,{"disambiguationData":[TD([[subQ44,1.0]])],"derivedFrom":subQ0}),1.0]])]});}
            var Q2;
            Q2=makeQuery(id+"F18.imprint","IMPRINT",FACE,{"disambiguationData":[TD([[makeQuery(id+"F18.imprint","IMPRINT",EDGE,{"derivedFrom":sQuery(id+"F18.wireOp",EDGE,"E34")}),1.0]])]});
            loft(context, id + "F20", {"operationType" : NewBodyOperationType.ADD, "sheetProfilesArray" : [{ "sheetProfileEntities" : qUnion([Q1]) }, { "sheetProfileEntities" : qUnion([Q2]) }]});
        }
        {
            var Q0;
            {var subQ3=sQuery(id+"F0.wireOp",EDGE,"E0.bottom");Q0=makeQuery(id+"F15.imprint","IMPRINT",FACE,{"disambiguationData":[TD([[makeQuery(id+"F15.imprint","IMPRINT",EDGE,{"derivedFrom":makeQuery(id+"F1.opExtrude","CAP_EDGE",EDGE,{"disambiguationData":[OSD([subQ3])],"isStart":false})}),-1.0]])]});}
            var sketch = newSketch(context, id + "F21", { "sketchPlane" : qUnion([Q0])});
            skLineSegment(sketch, "E36.bottom", {"start": v(-61.6, -5) * mm, "end": v(-60, -5) * mm});
            skLineSegment(sketch, "E36.top", {"start": v(-61.6, -20) * mm, "end": v(-60, -20) * mm});
            skLineSegment(sketch, "E36.left", {"start": v(-61.6, -5) * mm, "end": v(-61.6, -20) * mm});
            skLineSegment(sketch, "E36.right", {"start": v(-60, -5) * mm, "end": v(-60, -20) * mm});
            skLineSegment(sketch, "E37.bottom", {"start": v(-61.6, -93) * mm, "end": v(-60, -93) * mm});
            skLineSegment(sketch, "E37.top", {"start": v(-61.6, -108) * mm, "end": v(-60, -108) * mm});
            skLineSegment(sketch, "E37.left", {"start": v(-61.6, -93) * mm, "end": v(-61.6, -108) * mm});
            skLineSegment(sketch, "E37.right", {"start": v(-60, -93) * mm, "end": v(-60, -108) * mm});
            skLineSegment(sketch, "E38.bottom", {"start": v(60, -5) * mm, "end": v(61.6, -5) * mm});
            skLineSegment(sketch, "E38.top", {"start": v(60, -20) * mm, "end": v(61.6, -20) * mm});
            skLineSegment(sketch, "E38.left", {"start": v(60, -5) * mm, "end": v(60, -20) * mm});
            skLineSegment(sketch, "E38.right", {"start": v(61.6, -5) * mm, "end": v(61.6, -20) * mm});
            skLineSegment(sketch, "E39.bottom", {"start": v(60, -93) * mm, "end": v(61.6, -93) * mm});
            skLineSegment(sketch, "E39.top", {"start": v(60, -108) * mm, "end": v(61.6, -108) * mm});
            skLineSegment(sketch, "E39.left", {"start": v(60, -93) * mm, "end": v(60, -108) * mm});
            skLineSegment(sketch, "E39.right", {"start": v(61.6, -93) * mm, "end": v(61.6, -108) * mm});
            skLineSegment(sketch, "E40.bottom", {"start": v(-50, 1.6) * mm, "end": v(-35, 1.6) * mm});
            skLineSegment(sketch, "E40.top", {"start": v(-50, 0) * mm, "end": v(-35, 0) * mm});
            skLineSegment(sketch, "E40.left", {"start": v(-50, 1.6) * mm, "end": v(-50, 0) * mm});
            skLineSegment(sketch, "E40.right", {"start": v(-35, 1.6) * mm, "end": v(-35, 0) * mm});
            skLineSegment(sketch, "E41.bottom", {"start": v(35, 1.6) * mm, "end": v(50, 1.6) * mm});
            skLineSegment(sketch, "E41.top", {"start": v(35, 0) * mm, "end": v(50, 0) * mm});
            skLineSegment(sketch, "E41.left", {"start": v(35, 1.6) * mm, "end": v(35, 0) * mm});
            skLineSegment(sketch, "E41.right", {"start": v(50, 1.6) * mm, "end": v(50, 0) * mm});
            skSolve(sketch);
        }
        {
            var Q0;
            {var subQ3=sQuery(id+"F0.wireOp",EDGE,"E0.bottom");Q0=makeQuery(id+"F15.imprint","IMPRINT",FACE,{"disambiguationData":[TD([[makeQuery(id+"F15.imprint","IMPRINT",EDGE,{"derivedFrom":makeQuery(id+"F1.opExtrude","CAP_EDGE",EDGE,{"disambiguationData":[OSD([subQ3])],"isStart":false})}),-1.0]])]});}
            var sketch = newSketch(context, id + "F22", { "sketchPlane" : qUnion([Q0])});
            skCircle(sketch, "E42", {"center": v(-57, -110) * mm, "radius": 1.8 * mm});
            skCircle(sketch, "E43", {"center": v(57, -110) * mm, "radius": 1.8 * mm});
            skCircle(sketch, "E44", {"center": v(-57, -18) * mm, "radius": 1.8 * mm});
            skCircle(sketch, "E45", {"center": v(57, -18) * mm, "radius": 1.8 * mm});
            skCircle(sketch, "E46", {"center": v(-56.6, -3) * mm, "radius": 1.8 * mm});
            skCircle(sketch, "E47", {"center": v(56.6, -3) * mm, "radius": 1.8 * mm});
            skCircle(sketch, "E48", {"center": v(0, -3) * mm, "radius": 1.8 * mm});
            skSolve(sketch);
        }
        {
            var Q0;
            Q0 = qSketchRegion(id + "F22", true);
            extrude(context, id + "F23", {"entities" : qUnion([Q0]), "operationType" : NewBodyOperationType.ADD, "depth" : 3 * mm});
        }
        {
            var Q0;
            Q0 = qSketchRegion(id + "F3", true);
            extrude(context, id + "F24", {"entities" : qUnion([Q0]), "operationType" : NewBodyOperationType.ADD, "depth" : 13 * mm});
        }
        {
            var Q0;
            Q0=makeQuery(id+"F24.opExtrude","CAP_FACE",FACE,{"disambiguationData":[OSD([sQuery(id+"F3.wireOp",EDGE,"E2.bottom"),sQuery(id+"F3.wireOp",EDGE,"E2.top"),sQuery(id+"F3.wireOp",EDGE,"E2.left"),sQuery(id+"F3.wireOp",EDGE,"E2.right")])],"isStart":false});
            var Q1;
            Q1=makeQuery(id+"F24.opExtrude","SWEPT_EDGE",EDGE,{"disambiguationData":[OSD([sQuery(id+"F3.wireOp",EDGE,"E2.top"),sQuery(id+"F3.wireOp",EDGE,"E2.left")])]});
            var Q2;
            Q2=makeQuery(id+"F24.opExtrude","SWEPT_EDGE",EDGE,{"disambiguationData":[OSD([sQuery(id+"F3.wireOp",EDGE,"E2.top"),sQuery(id+"F3.wireOp",EDGE,"E2.right")])]});
            var Q3;
            Q3=makeQuery(id+"F24.opExtrude","SWEPT_EDGE",EDGE,{"disambiguationData":[OSD([sQuery(id+"F3.wireOp",EDGE,"E2.bottom"),sQuery(id+"F3.wireOp",EDGE,"E2.right")])]});
            var Q4;
            Q4=makeQuery(id+"F24.opExtrude","SWEPT_EDGE",EDGE,{"disambiguationData":[OSD([sQuery(id+"F3.wireOp",EDGE,"E2.bottom"),sQuery(id+"F3.wireOp",EDGE,"E2.left")])]});
            fillet(context, id + "F25", {"entities" : qUnion([Q0, Q1, Q2, Q3, Q4]), "radius" : 3 * mm, "tangentPropagation" : true, "allowEdgeOverflow" : false});
        }
    });
